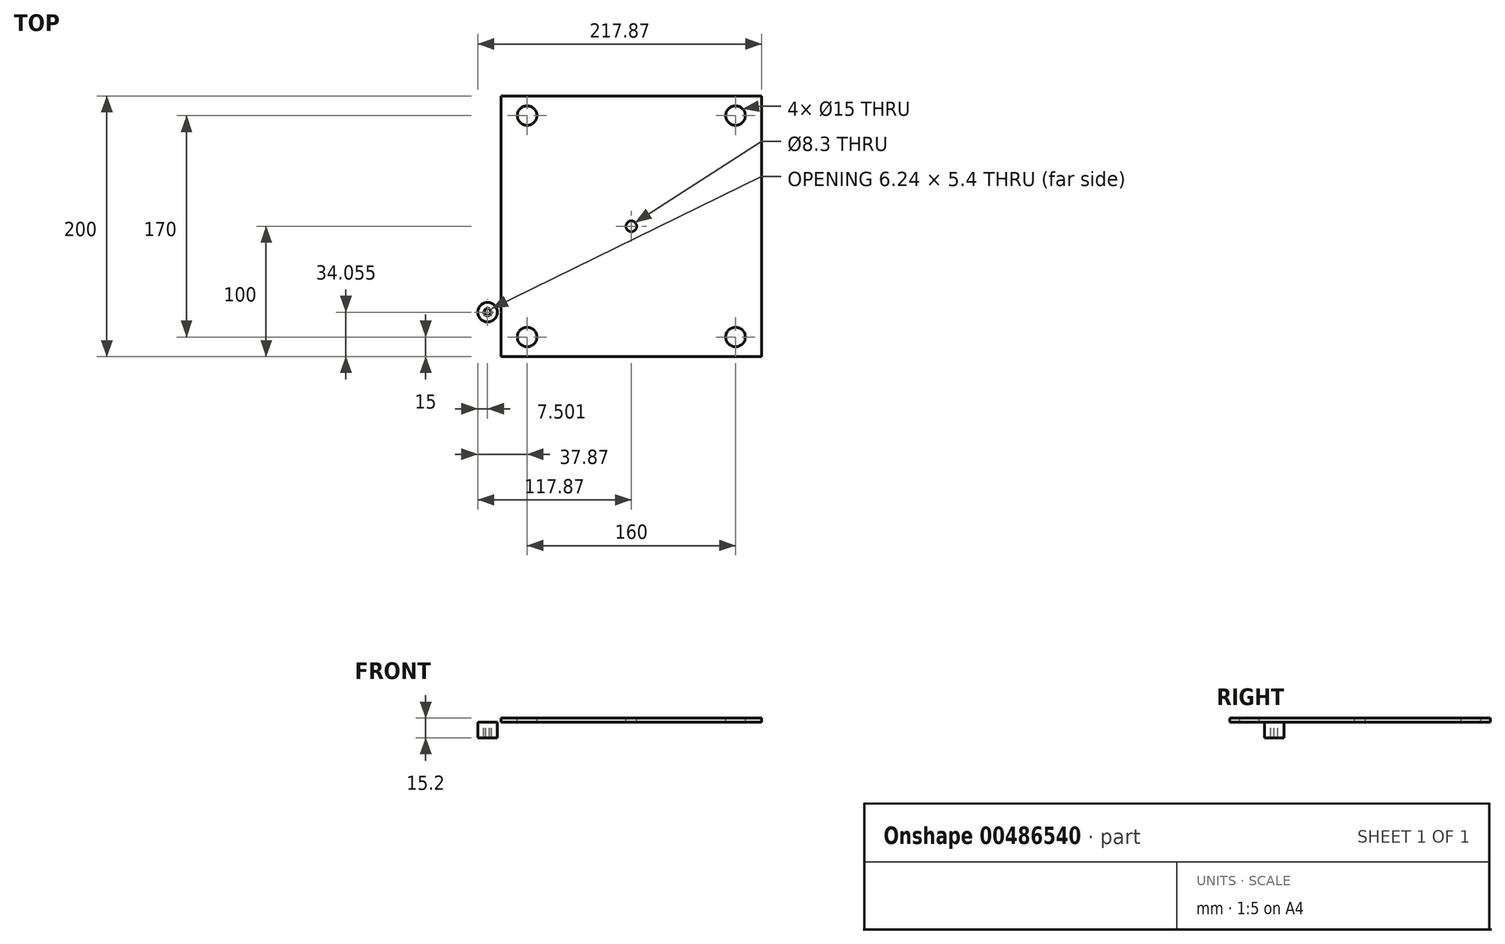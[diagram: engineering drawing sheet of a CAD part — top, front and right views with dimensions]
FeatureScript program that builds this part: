
annotation { "Feature Type Name" : "Feature", "Feature Type Description" : "" }
export const myFeature = defineFeature(function(context is Context, id is Id, definition is map)
    precondition{}
    {
        {
            var Q0;
            Q0=qCreatedBy(makeId("Top.planeOp"),FACE);
            var sketch = newSketch(context, id + "F0", { "sketchPlane" : qUnion([Q0])});
            skLineSegment(sketch, "E0.bottom", {"start": v(-100, 137.47) * mm, "end": v(100, 137.47) * mm});
            skLineSegment(sketch, "E0.top", {"start": v(-100, -62.53) * mm, "end": v(100, -62.53) * mm});
            skLineSegment(sketch, "E0.left", {"start": v(-100, 137.47) * mm, "end": v(-100, -62.53) * mm});
            skLineSegment(sketch, "E0.right", {"start": v(100, 137.47) * mm, "end": v(100, -62.53) * mm});
            skCircle(sketch, "E1", {"center": v(80, 122.47) * mm, "radius": 7.5 * mm});
            skCircle(sketch, "E2", {"center": v(0, 37.47) * mm, "radius": 4.15 * mm});
            skCircle(sketch, "E3", {"center": v(80, 122.47) * mm, "radius": 1.65 * mm});
            skCircle(sketch, "E4", {"center": v(80, 122.47) * mm, "radius": 2.25 * mm});
            skCircle(sketch, "E5.cCircle", {"center": v(80, 122.47) * mm, "radius": 2.7 * mm, "construction": true});
            skLineSegment(sketch, "E5.0", {"start": v(78.44, 125.17) * mm, "end": v(81.56, 125.17) * mm});
            skLineSegment(sketch, "E5.1", {"start": v(81.56, 125.17) * mm, "end": v(83.12, 122.47) * mm});
            skLineSegment(sketch, "E5.2", {"start": v(83.12, 122.47) * mm, "end": v(81.56, 119.77) * mm});
            skLineSegment(sketch, "E5.3", {"start": v(81.56, 119.77) * mm, "end": v(78.44, 119.77) * mm});
            skLineSegment(sketch, "E5.4", {"start": v(78.44, 119.77) * mm, "end": v(76.88, 122.47) * mm});
            skLineSegment(sketch, "E5.5", {"start": v(76.88, 122.47) * mm, "end": v(78.44, 125.17) * mm});
            skPoint(sketch, "E5.0.midPoint", {"position": v(80, 125.17) * mm});
            skCircle(sketch, "E6", {"center": v(80, -47.53) * mm, "radius": 7.5 * mm});
            skCircle(sketch, "E7", {"center": v(80, -47.53) * mm, "radius": 1.65 * mm});
            skCircle(sketch, "E8", {"center": v(80, -47.53) * mm, "radius": 2.25 * mm});
            skCircle(sketch, "E9.cCircle", {"center": v(80, -47.53) * mm, "radius": 2.7 * mm, "construction": true});
            skLineSegment(sketch, "E9.0", {"start": v(78.44, -44.83) * mm, "end": v(81.56, -44.83) * mm});
            skLineSegment(sketch, "E9.1", {"start": v(81.56, -44.83) * mm, "end": v(83.12, -47.53) * mm});
            skLineSegment(sketch, "E9.2", {"start": v(83.12, -47.53) * mm, "end": v(81.56, -50.23) * mm});
            skLineSegment(sketch, "E9.3", {"start": v(81.56, -50.23) * mm, "end": v(78.44, -50.23) * mm});
            skLineSegment(sketch, "E9.4", {"start": v(78.44, -50.23) * mm, "end": v(76.88, -47.53) * mm});
            skLineSegment(sketch, "E9.5", {"start": v(76.88, -47.53) * mm, "end": v(78.44, -44.83) * mm});
            skPoint(sketch, "E9.0.midPoint", {"position": v(80, -44.83) * mm});
            skCircle(sketch, "E10", {"center": v(-80, -47.53) * mm, "radius": 7.5 * mm});
            skCircle(sketch, "E11", {"center": v(-80, -47.53) * mm, "radius": 1.65 * mm});
            skCircle(sketch, "E12", {"center": v(-80, -47.53) * mm, "radius": 2.25 * mm});
            skCircle(sketch, "E13.cCircle", {"center": v(-80, -47.53) * mm, "radius": 2.7 * mm, "construction": true});
            skLineSegment(sketch, "E13.0", {"start": v(-81.56, -44.83) * mm, "end": v(-78.44, -44.83) * mm});
            skLineSegment(sketch, "E13.1", {"start": v(-78.44, -44.83) * mm, "end": v(-76.88, -47.53) * mm});
            skLineSegment(sketch, "E13.2", {"start": v(-76.88, -47.53) * mm, "end": v(-78.44, -50.23) * mm});
            skLineSegment(sketch, "E13.3", {"start": v(-78.44, -50.23) * mm, "end": v(-81.56, -50.23) * mm});
            skLineSegment(sketch, "E13.4", {"start": v(-81.56, -50.23) * mm, "end": v(-83.12, -47.53) * mm});
            skLineSegment(sketch, "E13.5", {"start": v(-83.12, -47.53) * mm, "end": v(-81.56, -44.83) * mm});
            skPoint(sketch, "E13.0.midPoint", {"position": v(-80, -44.83) * mm});
            skCircle(sketch, "E14", {"center": v(-80, 122.47) * mm, "radius": 7.5 * mm});
            skCircle(sketch, "E15", {"center": v(-80, 122.47) * mm, "radius": 1.65 * mm});
            skCircle(sketch, "E16", {"center": v(-80, 122.47) * mm, "radius": 2.25 * mm});
            skCircle(sketch, "E17.cCircle", {"center": v(-80, 122.47) * mm, "radius": 2.7 * mm, "construction": true});
            skLineSegment(sketch, "E17.0", {"start": v(-81.56, 125.17) * mm, "end": v(-78.44, 125.17) * mm});
            skLineSegment(sketch, "E17.1", {"start": v(-78.44, 125.17) * mm, "end": v(-76.88, 122.47) * mm});
            skLineSegment(sketch, "E17.2", {"start": v(-76.88, 122.47) * mm, "end": v(-78.44, 119.77) * mm});
            skLineSegment(sketch, "E17.3", {"start": v(-78.44, 119.77) * mm, "end": v(-81.56, 119.77) * mm});
            skLineSegment(sketch, "E17.4", {"start": v(-81.56, 119.77) * mm, "end": v(-83.12, 122.47) * mm});
            skLineSegment(sketch, "E17.5", {"start": v(-83.12, 122.47) * mm, "end": v(-81.56, 125.17) * mm});
            skPoint(sketch, "E17.0.midPoint", {"position": v(-80, 125.17) * mm});
            skText(sketch, "E18", { "text": "Marcela Ixquiac  Carnet: 17258\nHans Burmester Carnet: 17022\nLuis Velasquez    Carnet: 17207", "fontName": "OpenSans-Regular.ttf"});
            const initialGuessF0  = {"E18": [-0.15965, -0.11364, 1, 0, 0.02616]};
            skSetInitialGuess(sketch, initialGuessF0);
            skSolve(sketch);
        }
        {
            var Q0;
            Q0=makeQuery(id+"F0.imprint","IMPRINT",FACE,{"disambiguationData":[TD([[makeQuery(id+"F0.imprint","IMPRINT",EDGE,{"derivedFrom":sQuery(id+"F0.wireOp",EDGE,"E0.bottom")}),-1.0]])]});
            extrude(context, id + "F1", {"entities" : qUnion([Q0]), "oppositeDirection" : true, "depth" : 3.2 * mm, "offsetDistance" : 25 * mm});
        }
        {
            var Q0;
            Q0=makeQuery(id+"F1.opExtrude","CAP_FACE",FACE,{"disambiguationData":[OSD([sQuery(id+"F0.wireOp",EDGE,"E0.bottom"),sQuery(id+"F0.wireOp",EDGE,"E0.top"),sQuery(id+"F0.wireOp",EDGE,"E0.left"),sQuery(id+"F0.wireOp",EDGE,"E0.right"),sQuery(id+"F0.wireOp",EDGE,"E1"),sQuery(id+"F0.wireOp",EDGE,"E2"),sQuery(id+"F0.wireOp",EDGE,"E6"),sQuery(id+"F0.wireOp",EDGE,"E10"),sQuery(id+"F0.wireOp",EDGE,"E14")])],"isStart":false});
            var sketch = newSketch(context, id + "F2", { "sketchPlane" : qUnion([Q0])});
            skCircle(sketch, "E19", {"center": v(-110.37, 28.47) * mm, "radius": 7.5 * mm});
            skCircle(sketch, "E20.cCircle", {"center": v(-110.37, 28.47) * mm, "radius": 2.7 * mm, "construction": true});
            skLineSegment(sketch, "E20.0", {"start": v(-111.93, 31.18) * mm, "end": v(-108.8, 31.18) * mm});
            skLineSegment(sketch, "E20.1", {"start": v(-108.8, 31.18) * mm, "end": v(-107.25, 28.47) * mm});
            skLineSegment(sketch, "E20.2", {"start": v(-107.25, 28.47) * mm, "end": v(-108.8, 25.77) * mm});
            skLineSegment(sketch, "E20.3", {"start": v(-108.8, 25.77) * mm, "end": v(-111.93, 25.77) * mm});
            skLineSegment(sketch, "E20.4", {"start": v(-111.93, 25.77) * mm, "end": v(-113.49, 28.47) * mm});
            skLineSegment(sketch, "E20.5", {"start": v(-113.49, 28.47) * mm, "end": v(-111.93, 31.18) * mm});
            skPoint(sketch, "E20.0.midPoint", {"position": v(-110.37, 31.18) * mm});
            skCircle(sketch, "E21", {"center": v(-110.37, 28.47) * mm, "radius": 2.3 * mm});
            skCircle(sketch, "E22", {"center": v(-110.37, 28.47) * mm, "radius": 1.65 * mm});
            skSolve(sketch);
        }
        {
            var Q0;
            Q0=makeQuery(id+"F2.imprint","IMPRINT",FACE,{"disambiguationData":[TD([[makeQuery(id+"F2.imprint","IMPRINT",EDGE,{"derivedFrom":sQuery(id+"F2.wireOp",EDGE,"E19")}),1.0]])]});
            extrude(context, id + "F3", {"entities" : qUnion([Q0]), "depth" : 12 * mm, "offsetDistance" : 25 * mm});
        }
    });
